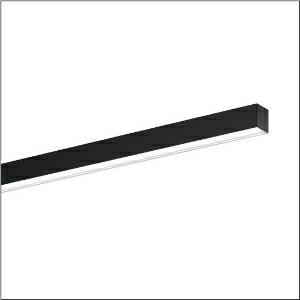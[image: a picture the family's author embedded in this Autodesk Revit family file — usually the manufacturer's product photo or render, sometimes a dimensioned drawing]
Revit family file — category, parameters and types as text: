
# Revit family: silica_r__21_51mx23da34bb_8ce5
name_source: partatom
category: Lighting Fixtures
units: mm (PartAtom-declared; Revit-internal decimal feet)

## family parameters
Cut with Voids When Loaded = No
Host = Face
Light Source = No
Part Type = Normal
Room Calculation Point = No
Round Connector Dimension = Use Diameter
Shared = No

## types (1)
- --- (1 x LED, 3280 lm, 24.1 W, 3000K)
    Apparent Load = 24 VA
    CIE Flux Codes = 78 96 99 100 100
    Color Rendering = 80
    Color Temperature = 3000K
    Default Elevation = 1800 mm
    Description = Silica® 21, office luminaire, primary optical cover: prismatic diffuser, of PMMA, CAT 2 (L<= 3000cd/m²), light emission: direct distribution, primary light characteristic: symmetric, installation type: surface-mounted, LED, rated luminous flux: 3.280lm, luminous efficacy: 136lm/W, light colour: 830, colour temperature: 3000K, control gear: DALI 2, with terminal, 3+2-pole, max. 2.5mm², mains connection: 220..240V, AC, 50/60Hz, rated input power: 24.1W, luminaire housing, of aluminium, matt jet black (RAL 9005), length: 1.204mm, width: 53mm, height: 53mm, protection rating (complete): IP20, insulation class (complete): insulation class I (protective earthing), certification: CE, permissible operating ambient temperature: 0..+35°C, standard: EN 50419, packaging unit: 1 piece
    Height = 53 mm
    Lamp = 1 x LED
    Lamp Light Flux = 3280 lm
    Lamp Power = 24.1 W
    Lamp count = 1
    Length = 1204 mm
    Luminous efficacy = 136 lm/W
    Manufacturer = Siteco
    ModVariant = No
    Model = 51MX23DA34BB
    Mounting Place = Ceiling
    Mounting Type = Surface mounted
    Number of Poles = 1
    OnlyDefault = Yes
    Power Factor = 1
    Product Name = Silica® 21
    Product group = office luminaire | ceiling mounted
    ProductGroupID = 302
    Protection Class = Protection class I
    Protection Degree = IP 20
    RLX_Detail_Level = 1
    RLX_Emergency_Light_Flux = 0 lm
    RLX_Emergency_Type = 0
    RLX_Emergency_Type_DB = No
    RlxData = <blob elided: 23725 chars, md5=55240c01>
    Socket = socket
    Standby Power = 0 W
    System Light Flux = 3280 lm
    System Power = 24 W
    Type Comments = factory setting: luminous flux: 100 % | dim-lin: 254 | 345 mA
    Type Image = l_1335925.jpg
    URL = http://relux.com
    VarID = @adj_007911
    Voltage = 0 V
    Weight = 0.00 kg
    Width = 53 mm

## geometry (parser evidence)
native form markers: Blend x4, Sweep x9
no freeform markers — native parametric forms only
